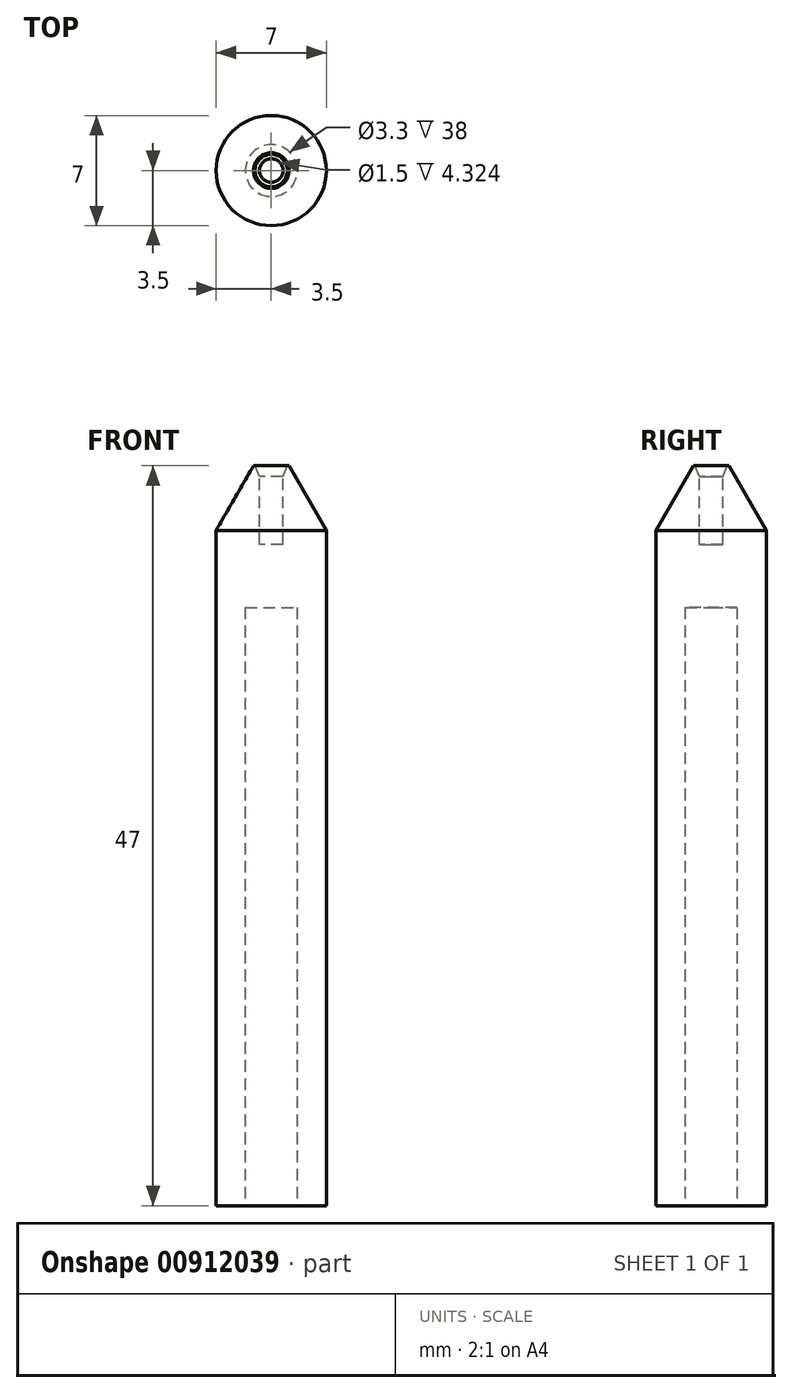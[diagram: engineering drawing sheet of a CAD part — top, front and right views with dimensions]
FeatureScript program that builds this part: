
annotation { "Feature Type Name" : "Feature", "Feature Type Description" : "" }
export const myFeature = defineFeature(function(context is Context, id is Id, definition is map)
    precondition{}
    {
        {
            var Q0;
            Q0=qCreatedBy(makeId("Top.planeOp"),FACE);
            var sketch = newSketch(context, id + "F0", { "sketchPlane" : qUnion([Q0])});
            skCircle(sketch, "E0", {"center": v(0, 0) * mm, "radius": 3.5 * mm});
            skSolve(sketch);
        }
        {
            var Q0;
            Q0=makeQuery(id+"F0.imprint","IMPRINT",FACE,{"disambiguationData":[TD([[makeQuery(id+"F0.imprint","IMPRINT",EDGE,{"derivedFrom":sQuery(id+"F0.wireOp",EDGE,"VMIiSX6W-2FtX-6may-WHbP-bbm3xMGcCuNN")}),1.0]])]});
            var Q1;
            Q1=makeQuery(id+"F0.imprint","IMPRINT",FACE,{"disambiguationData":[TD([[makeQuery(id+"F0.imprint","IMPRINT",EDGE,{"derivedFrom":sQuery(id+"F0.wireOp",EDGE,"E0")}),1.0]])]});
            extrude(context, id + "F1", {"entities" : qUnion([Q0, Q1]), "depth" : 25 * mm, "offsetDistance" : 25 * mm});
        }
        {
            var Q0;
            Q0 = qSketchRegion(id + "F0", true);
            extrude(context, id + "F2", {"entities" : qUnion([Q0]), "depth" : 47 * mm, "offsetDistance" : 25 * mm});
        }
        {
            var Q0;
            Q0=makeQuery(id+"F2.opExtrude","CAP_FACE",FACE,{"disambiguationData":[OSD([sQuery(id+"F0.wireOp",EDGE,"E0")])],"isStart":true});
            var sketch = newSketch(context, id + "F3", { "sketchPlane" : qUnion([Q0])});
            skCircle(sketch, "E1", {"center": v(0, 0) * mm, "radius": 1.65 * mm});
            skSolve(sketch);
        }
        {
            var Q0;
            Q0 = qSketchRegion(id + "F3", true);
            extrude(context, id + "F4", {"entities" : qUnion([Q0]), "operationType" : NewBodyOperationType.REMOVE, "oppositeDirection" : true, "depth" : 38 * mm, "offsetDistance" : 25 * mm});
        }
        {
            var Q0;
            Q0=makeQuery(id+"F2.opExtrude","CAP_FACE",FACE,{"disambiguationData":[OSD([sQuery(id+"F0.wireOp",EDGE,"E0")])],"isStart":false});
            var sketch = newSketch(context, id + "F5", { "sketchPlane" : qUnion([Q0])});
            skCircle(sketch, "E2", {"center": v(0, 0) * mm, "radius": 1.13 * mm});
            skSolve(sketch);
        }
        {
            var Q0;
            Q0 = qSketchRegion(id + "F5", true);
            extrude(context, id + "F6", {"entities" : qUnion([Q0]), "operationType" : NewBodyOperationType.INTERSECT, "oppositeDirection" : true, "depth" : 100 * mm, "offsetDistance" : 25 * mm, "hasDraft" : true, "draftAngle" : 30 * degree});
        }
        {
            var Q0;
            Q0=makeQuery(id+"F1.opExtrude","SWEPT_BODY",BODY,{"disambiguationData":[OSD([sQuery(id+"F0.wireOp",EDGE,"E0")])]});
            deleteBodies(context, id + "F7", {"entities" : qUnion([Q0])});
        }
        {
            var Q0;
            Q0=makeQuery(id+"F2.opExtrude","CAP_FACE",FACE,{"disambiguationData":[OSD([sQuery(id+"F0.wireOp",EDGE,"E0")])],"isStart":false});
            var sketch = newSketch(context, id + "F8", { "sketchPlane" : qUnion([Q0])});
            skCircle(sketch, "E3", {"center": v(0, 0) * mm, "radius": 1.03 * mm});
            skSolve(sketch);
        }
        {
            var Q0;
            Q0=makeQuery(id+"F8.imprint","IMPRINT",FACE,{"disambiguationData":[TD([[makeQuery(id+"F8.imprint","IMPRINT",EDGE,{"derivedFrom":sQuery(id+"F8.wireOp",EDGE,"E3")}),1.0]])]});
            extrude(context, id + "F9", {"entities" : qUnion([Q0]), "operationType" : NewBodyOperationType.REMOVE, "oppositeDirection" : true, "depth" : 2 * mm, "offsetDistance" : 25 * mm, "hasDraft" : true, "draftAngle" : 22.5 * degree, "draftPullDirection" : true});
        }
        {
            var Q0;
            Q0=makeQuery(id+"F2.opExtrude","CAP_FACE",FACE,{"disambiguationData":[OSD([sQuery(id+"F0.wireOp",EDGE,"E0")])],"isStart":false});
            var sketch = newSketch(context, id + "F10", { "sketchPlane" : qUnion([Q0])});
            skCircle(sketch, "E4", {"center": v(0, 0) * mm, "radius": 0.75 * mm});
            skSolve(sketch);
        }
        {
            var Q0;
            Q0=makeQuery(id+"F10.imprint","IMPRINT",FACE,{"disambiguationData":[TD([[makeQuery(id+"F10.imprint","IMPRINT",EDGE,{"derivedFrom":sQuery(id+"F10.wireOp",EDGE,"E4")}),1.0]])]});
            extrude(context, id + "F11", {"entities" : qUnion([Q0]), "operationType" : NewBodyOperationType.REMOVE, "oppositeDirection" : true, "depth" : 5 * mm, "offsetDistance" : 25 * mm});
        }
    });
